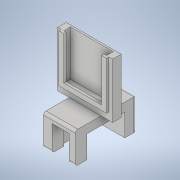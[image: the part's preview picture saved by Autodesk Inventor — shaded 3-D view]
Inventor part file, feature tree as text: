
AUTODESK INVENTOR PART (.ipt)
format: ipt  version: 2022 (Build 260153000, 153)  size: 221,696 bytes
history: native  units: mm
features: extrude x8, sketch x8, fillet x1
ambient origin geometry x8: Origin, YZ Plane, XZ Plane, XY Plane, X Axis, Y Axis, Z Axis, Center Point
bodies: Solid1 (feature_tree)
feature tree (17):
  extrude  "Extrusion1"  Depth=50.0mm
  extrude  "Extrusion2"  Depth=42.0mm
  extrude  "Extrusion3"  Depth=37.5mm
  extrude  "Extrusion6"  Depth=21.0mm TaperAngle=0.0deg
  fillet  "Fillet1"  Radius=14.0mm
  extrude  "Extrusion8"  Depth=21.0mm TaperAngle=0.0deg
  extrude  "Extrusion9"  Depth=6.0mm
  extrude  "Extrusion10"  Depth=18.0mm
  extrude  "Extrusion11"  Depth=2.0mm
  sketch  "Sketch1"  dims[d0=25.4mm d1=50.0mm]
  sketch  "Sketch2"  dims[d2=5.0mm d3=0.0mm d4=42.0mm]
  sketch  "Sketch3"  dims[d5=15.2mm d6=37.5mm]
  sketch  "Sketch6"  dims[d7=31.0mm d8=21.0mm d9=0.0mm d10=14.0mm]
  sketch  "Sketch8"  dims[d11=2.0mm d12=21.0mm d13=0.0mm]
  sketch  "Sketch9"  dims[d14=7.0mm d24=6.0mm]
  sketch  "Sketch10"  dims[d25=9.55mm d26=18.0mm]
  sketch  "Sketch11"  dims[d27=25.4mm d28=0.0mm d29=2.0mm d33=22.5mm d34=22.5mm d35=4.0mm d36=3.0mm d37=45.0mm d38=0.0mm d39=17.5mm d40=17.5mm d41=37.0mm d42=0.0mm d43=2.0mm d44=0.0mm d45=2.0mm d46=2.0mm d48=2.0mm d49=35.0mm d50=31.0mm d51=2.0mm d52=0.0mm]
